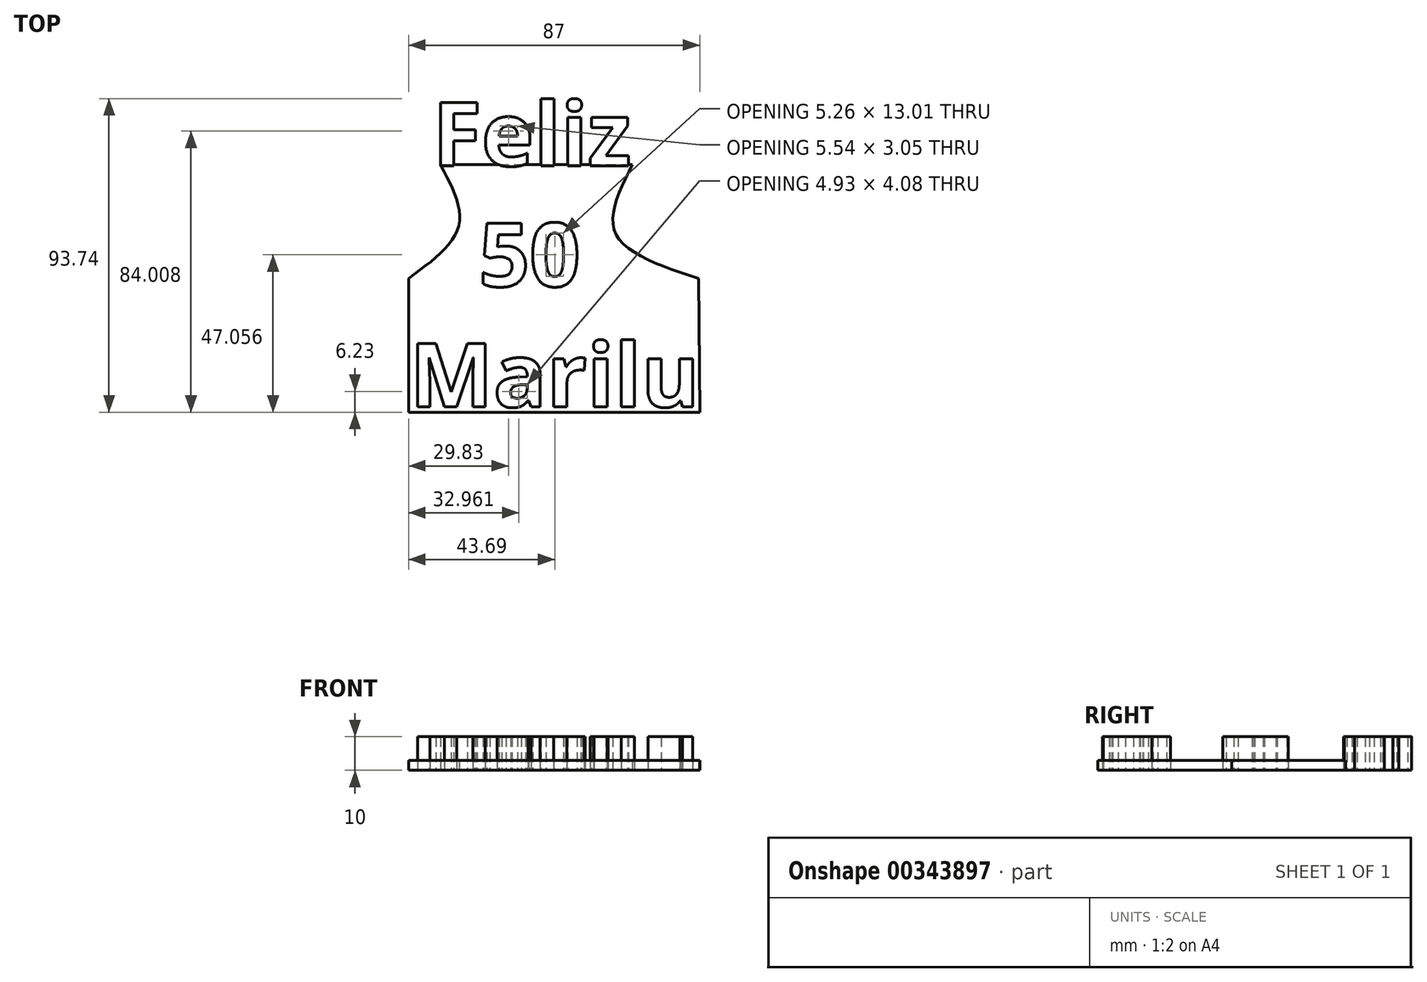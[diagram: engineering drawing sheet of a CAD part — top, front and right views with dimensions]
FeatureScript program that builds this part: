
annotation { "Feature Type Name" : "Feature", "Feature Type Description" : "" }
export const myFeature = defineFeature(function(context is Context, id is Id, definition is map)
    precondition{}
    {
        {
            var Q0;
            Q0=qCreatedBy(makeId("Top.planeOp"),FACE);
            var sketch = newSketch(context, id + "F0", { "sketchPlane" : qUnion([Q0])});
            skText(sketch, "E0", { "text": "   Feliz\n     50\n  Marilu ", "fontName": "OpenSans-Bold.ttf"});
            skFitSpline(sketch, "E1", {"points": [v(0, 0) * mm, v(-26.9, -27.29) * mm, v(0, -55.2) * mm, v(0, -75.18) * mm], "startDerivative": vector(-118.48, -74.07) * mm, "endDerivative": vector(-24.72, -75.35) * mm});
            skLineSegment(sketch, "E2", {"start": v(0, -75.18) * mm, "end": v(-89.65, -75.18) * mm});
            skFitSpline(sketch, "E3", {"points": [v(-100, 0) * mm, v(-74.03, -28.31) * mm, v(-97.34, -54.69) * mm, v(-89.65, -75.18) * mm], "startDerivative": vector(124.17, -71.1) * mm, "endDerivative": vector(59.31, -73.58) * mm});
            const initialGuessF0  = {"E0": [-0.1, 0, 1, 0, 0.01907]};
            skSetInitialGuess(sketch, initialGuessF0);
            skSolve(sketch);
        }
        {
            var Q0;
            Q0 = qSketchRegion(id + "F0", true);
            extrude(context, id + "F1", {"entities" : qUnion([Q0]), "depth" : 10 * mm});
        }
        {
            var Q0;
            Q0=qCreatedBy(makeId("Top.planeOp"),FACE);
            var sketch = newSketch(context, id + "F2", { "sketchPlane" : qUnion([Q0])});
            skLineSegment(sketch, "E4", {"start": v(-86.6, -73.61) * mm, "end": v(0.4, -73.61) * mm});
            skLineSegment(sketch, "E5", {"start": v(-77.08, 0.34) * mm, "end": v(-19.79, 0.34) * mm});
            skLineSegment(sketch, "E6", {"start": v(-86.6, -73.61) * mm, "end": v(-86.6, -33.61) * mm});
            skLineSegment(sketch, "E7", {"start": v(0.4, -73.61) * mm, "end": v(0, -33.61) * mm});
            skFitSpline(sketch, "E8", {"points": [v(-86.6, -33.61) * mm, v(-71.62, -17.84) * mm, v(-77.08, 0.34) * mm], "startDerivative": vector(39.38, 28.66) * mm, "endDerivative": vector(-21.02, 39.37) * mm});
            skFitSpline(sketch, "E9", {"points": [v(0, -33.61) * mm, v(-24.85, -20.02) * mm, v(-19.79, 0.34) * mm], "startDerivative": vector(-61.59, 20.27) * mm, "endDerivative": vector(24.16, 48.34) * mm});
            skSolve(sketch);
        }
        {
            var Q0;
            Q0 = qSketchRegion(id + "F2", true);
            extrude(context, id + "F3", {"entities" : qUnion([Q0]), "depth" : 3 * mm});
        }
    });
